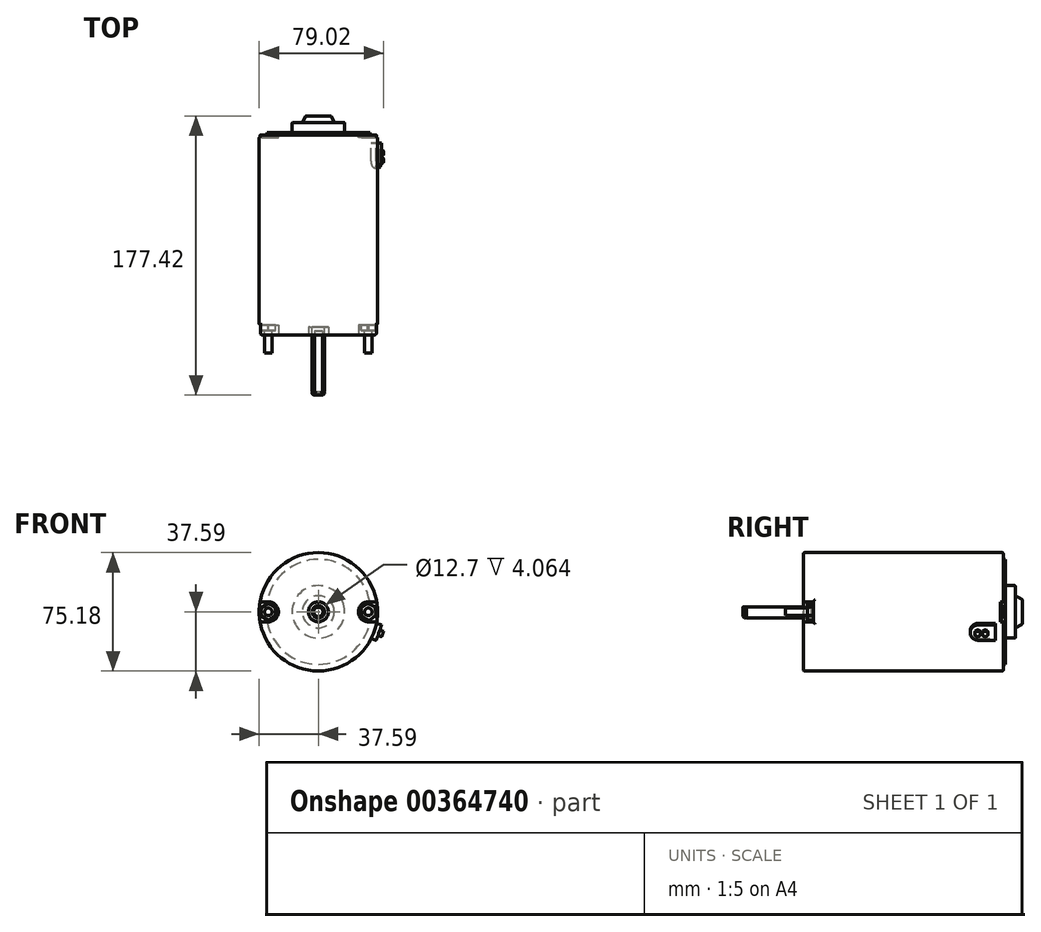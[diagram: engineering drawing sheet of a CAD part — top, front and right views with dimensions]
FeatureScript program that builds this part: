
annotation { "Feature Type Name" : "Feature", "Feature Type Description" : "" }
export const myFeature = defineFeature(function(context is Context, id is Id, definition is map)
    precondition{}
    {
        {
            var Q0;
            Q0=qCreatedBy(makeId("Front.planeOp"),FACE);
            var sketch = newSketch(context, id + "F0", { "sketchPlane" : qUnion([Q0])});
            skCircle(sketch, "E0", {"center": v(0, 0) * mm, "radius": 37.6 * mm});
            skSolve(sketch);
        }
        {
            var Q0;
            Q0 = qSketchRegion(id + "F0", true);
            extrude(context, id + "F1", {"entities" : qUnion([Q0]), "depth" : 127 * mm});
        }
        {
            var Q0;
            Q0=makeQuery(id+"F1.opExtrude","CAP_FACE",FACE,{"disambiguationData":[OSD([sQuery(id+"F0.wireOp",EDGE,"E0")])],"isStart":false});
            var sketch = newSketch(context, id + "F2", { "sketchPlane" : qUnion([Q0])});
            skCircle(sketch, "E1", {"center": v(0, 0) * mm, "radius": 6.35 * mm});
            skSolve(sketch);
        }
        {
            var Q0;
            Q0 = qSketchRegion(id + "F2", true);
            extrude(context, id + "F3", {"entities" : qUnion([Q0]), "operationType" : NewBodyOperationType.REMOVE, "oppositeDirection" : true, "depth" : 5.08 * mm});
        }
        {
            var Q0;
            Q0=makeQuery(id+"F3.boolean.opBoolean","COPY",FACE,{"derivedFrom":makeQuery(id+"F3.opExtrude","CAP_FACE",FACE,{"disambiguationData":[OSD([sQuery(id+"F2.wireOp",EDGE,"E1")])],"isStart":false})});
            var sketch = newSketch(context, id + "F4", { "sketchPlane" : qUnion([Q0])});
            skCircle(sketch, "E2", {"center": v(0, 0) * mm, "radius": 3.96 * mm});
            skSolve(sketch);
        }
        {
            var Q0;
            Q0 = qSketchRegion(id + "F4", true);
            extrude(context, id + "F5", {"entities" : qUnion([Q0]), "operationType" : NewBodyOperationType.ADD, "depth" : 43.43 * mm});
        }
        {
            var Q0;
            Q0=makeQuery(id+"F5.opExtrude","CAP_EDGE",EDGE,{"disambiguationData":[OSD([sQuery(id+"F4.wireOp",EDGE,"E2")])],"isStart":false});
            chamfer(context, id + "F6", {"entities" : qUnion([Q0]), "width" : 1.02 * mm, "tangentPropagation" : true});
        }
        {
            var Q0;
            Q0=makeQuery(id+"F5.opExtrude","CAP_FACE",FACE,{"disambiguationData":[OSD([sQuery(id+"F4.wireOp",EDGE,"E2")])],"isStart":false});
            var sketch = newSketch(context, id + "F7", { "sketchPlane" : qUnion([Q0])});
            skLineSegment(sketch, "E3", {"start": v(-2.56, 3.02) * mm, "end": v(2.56, 3.02) * mm});
            skArc(sketch, "E4.0", {"start": v(2.56, 3.02) * mm, "mid": v(0, 3.96) * mm, "end": v(-2.56, 3.02) * mm});
            skLineSegment(sketch, "E5", {"start": v(0, 3.02) * mm, "end": v(0, -3.96) * mm, "construction": true});
            skPoint(sketch, "E6.orphan", {"position": v(-4.9, 3.02) * mm});
            skPoint(sketch, "E7.orphan", {"position": v(4.9, 3.02) * mm});
            skSolve(sketch);
        }
        {
            var Q0;
            Q0 = qSketchRegion(id + "F7", true);
            var Q1;
            Q1=makeQuery(id+"F3.boolean.opBoolean","COPY",FACE,{"derivedFrom":makeQuery(id+"F3.opExtrude","CAP_FACE",FACE,{"disambiguationData":[OSD([sQuery(id+"F2.wireOp",EDGE,"E1")])],"isStart":false})});
            extrude(context, id + "F8", {"entities" : qUnion([Q0]), "operationType" : NewBodyOperationType.REMOVE, "oppositeDirection" : true, "endBoundEntityFace" : qUnion([Q1]), "depth" : 40.64 * mm});
        }
        {
            var Q0;
            Q0=makeQuery(id+"F5.opExtrude","CAP_FACE",FACE,{"disambiguationData":[OSD([sQuery(id+"F4.wireOp",EDGE,"E2")])],"isStart":false});
            cPlane(context, id + "F9", {"entities" : qUnion([Q0]), "cplaneType" : CPlaneType.OFFSET, "offset" : 1.6 * mm, "oppositeDirection" : true, "width" : 152.4 * mm, "height" : 152.4 * mm});
        }
        {
            var Q0;
            Q0=qCreatedBy(id+"F9.planeOp",FACE);
            var sketch = newSketch(context, id + "F10", { "sketchPlane" : qUnion([Q0])});
            skCircle(sketch, "E8", {"center": v(0, 0) * mm, "radius": 3.58 * mm});
            skCircle(sketch, "E9", {"center": v(0, 0) * mm, "radius": 4.9 * mm});
            skSolve(sketch);
        }
        {
            var Q0;
            Q0 = qSketchRegion(id + "F10", true);
            extrude(context, id + "F11", {"entities" : qUnion([Q0]), "operationType" : NewBodyOperationType.REMOVE, "oppositeDirection" : true, "depth" : 0.79 * mm});
        }
        {
            var Q0;
            Q0=makeQuery(id+"F1.opExtrude","CAP_FACE",FACE,{"disambiguationData":[OSD([sQuery(id+"F0.wireOp",EDGE,"E0")])],"isStart":false});
            var sketch = newSketch(context, id + "F12", { "sketchPlane" : qUnion([Q0])});
            skArc(sketch, "E10", {"start": v(31.75, 6.35) * mm, "mid": v(25.4, 0) * mm, "end": v(31.75, -6.35) * mm});
            skArc(sketch, "E11", {"start": v(-31.75, -6.35) * mm, "mid": v(-25.4, 0) * mm, "end": v(-31.75, 6.35) * mm});
            skLineSegment(sketch, "E12", {"start": v(-31.75, 0) * mm, "end": v(31.75, 0) * mm, "construction": true});
            skLineSegment(sketch, "E13", {"start": v(-31.75, -6.35) * mm, "end": v(-52.48, -6.35) * mm});
            skLineSegment(sketch, "E14", {"start": v(-52.48, -6.35) * mm, "end": v(-52.48, 6.35) * mm});
            skLineSegment(sketch, "E15", {"start": v(-52.48, 6.35) * mm, "end": v(-31.75, 6.35) * mm});
            skLineSegment(sketch, "E16", {"start": v(31.75, -6.35) * mm, "end": v(43.63, -6.35) * mm});
            skLineSegment(sketch, "E17", {"start": v(43.63, -6.35) * mm, "end": v(43.63, 6.35) * mm});
            skLineSegment(sketch, "E18", {"start": v(43.63, 6.35) * mm, "end": v(31.75, 6.35) * mm});
            skSolve(sketch);
        }
        {
            var Q0;
            Q0 = qSketchRegion(id + "F12", true);
            extrude(context, id + "F13", {"entities" : qUnion([Q0]), "operationType" : NewBodyOperationType.REMOVE, "oppositeDirection" : true, "depth" : 6.35 * mm});
        }
        {
            var Q0;
            Q0=makeQuery(id+"F1.opExtrude","CAP_FACE",FACE,{"disambiguationData":[OSD([sQuery(id+"F0.wireOp",EDGE,"E0")])],"isStart":false});
            fillet(context, id + "F14", {"entities" : qUnion([Q0]), "radius" : 1.02 * mm, "tangentPropagation" : true, "allowEdgeOverflow" : false});
        }
        {
            var Q0;
            Q0=makeQuery(id+"F13.boolean.opBoolean","INTERSECT",EDGE,{"derivedFrom":[makeQuery(id+"F1.opExtrude","SWEPT_FACE",FACE,{"disambiguationData":[OSD([sQuery(id+"F0.wireOp",EDGE,"E0")])]}),makeQuery(id+"F13.opExtrude","CAP_FACE",FACE,{"disambiguationData":[OSD([sQuery(id+"F12.wireOp",EDGE,"E11"),sQuery(id+"F12.wireOp",EDGE,"E13"),sQuery(id+"F12.wireOp",EDGE,"E14"),sQuery(id+"F12.wireOp",EDGE,"E15")])],"isStart":false})]});
            var Q1;
            Q1=makeQuery(id+"F13.boolean.opBoolean","INTERSECT",EDGE,{"derivedFrom":[makeQuery(id+"F1.opExtrude","SWEPT_FACE",FACE,{"disambiguationData":[OSD([sQuery(id+"F0.wireOp",EDGE,"E0")])]}),makeQuery(id+"F13.opExtrude","SWEPT_FACE",FACE,{"disambiguationData":[OSD([sQuery(id+"F12.wireOp",EDGE,"E15")])]})]});
            var Q2;
            Q2=makeQuery(id+"F13.boolean.opBoolean","INTERSECT",EDGE,{"derivedFrom":[makeQuery(id+"F1.opExtrude","SWEPT_FACE",FACE,{"disambiguationData":[OSD([sQuery(id+"F0.wireOp",EDGE,"E0")])]}),makeQuery(id+"F13.opExtrude","SWEPT_FACE",FACE,{"disambiguationData":[OSD([sQuery(id+"F12.wireOp",EDGE,"E13")])]})]});
            var Q3;
            Q3=makeQuery(id+"F13.boolean.opBoolean","INTERSECT",EDGE,{"derivedFrom":[makeQuery(id+"F1.opExtrude","SWEPT_FACE",FACE,{"disambiguationData":[OSD([sQuery(id+"F0.wireOp",EDGE,"E0")])]}),makeQuery(id+"F13.opExtrude","SWEPT_FACE",FACE,{"disambiguationData":[OSD([sQuery(id+"F12.wireOp",EDGE,"E16")])]})]});
            var Q4;
            Q4=makeQuery(id+"F13.boolean.opBoolean","INTERSECT",EDGE,{"derivedFrom":[makeQuery(id+"F1.opExtrude","SWEPT_FACE",FACE,{"disambiguationData":[OSD([sQuery(id+"F0.wireOp",EDGE,"E0")])]}),makeQuery(id+"F13.opExtrude","CAP_FACE",FACE,{"disambiguationData":[OSD([sQuery(id+"F12.wireOp",EDGE,"E10"),sQuery(id+"F12.wireOp",EDGE,"E16"),sQuery(id+"F12.wireOp",EDGE,"E17"),sQuery(id+"F12.wireOp",EDGE,"E18")])],"isStart":false})]});
            var Q5;
            Q5=makeQuery(id+"F13.boolean.opBoolean","INTERSECT",EDGE,{"derivedFrom":[makeQuery(id+"F1.opExtrude","SWEPT_FACE",FACE,{"disambiguationData":[OSD([sQuery(id+"F0.wireOp",EDGE,"E0")])]}),makeQuery(id+"F13.opExtrude","SWEPT_FACE",FACE,{"disambiguationData":[OSD([sQuery(id+"F12.wireOp",EDGE,"E18")])]})]});
            fillet(context, id + "F15", {"entities" : qUnion([Q0, Q1, Q2, Q3, Q4, Q5]), "radius" : 1.02 * mm, "tangentPropagation" : true, "allowEdgeOverflow" : false});
        }
        {
            var Q0;
            Q0=makeQuery(id+"F13.boolean.opBoolean","COPY",FACE,{"derivedFrom":makeQuery(id+"F13.opExtrude","CAP_FACE",FACE,{"disambiguationData":[OSD([sQuery(id+"F12.wireOp",EDGE,"E11"),sQuery(id+"F12.wireOp",EDGE,"E13"),sQuery(id+"F12.wireOp",EDGE,"E14"),sQuery(id+"F12.wireOp",EDGE,"E15")])],"isStart":false})});
            var sketch = newSketch(context, id + "F16", { "sketchPlane" : qUnion([Q0])});
            skCircle(sketch, "E19", {"center": v(-31.75, 0) * mm, "radius": 2.37 * mm});
            skCircle(sketch, "E20", {"center": v(31.75, 0) * mm, "radius": 2.37 * mm});
            skSolve(sketch);
        }
        {
            var Q0;
            Q0 = qSketchRegion(id + "F16", true);
            extrude(context, id + "F17", {"entities" : qUnion([Q0]), "operationType" : NewBodyOperationType.ADD, "depth" : 17.78 * mm});
        }
        {
            var Q0;
            Q0=makeQuery(id+"F13.boolean.opBoolean","COPY",FACE,{"derivedFrom":makeQuery(id+"F13.opExtrude","CAP_FACE",FACE,{"disambiguationData":[OSD([sQuery(id+"F12.wireOp",EDGE,"E11"),sQuery(id+"F12.wireOp",EDGE,"E13"),sQuery(id+"F12.wireOp",EDGE,"E14"),sQuery(id+"F12.wireOp",EDGE,"E15")])],"isStart":false})});
            var sketch = newSketch(context, id + "F18", { "sketchPlane" : qUnion([Q0])});
            skCircle(sketch, "E21.cCircle", {"center": v(-31.75, 0) * mm, "radius": 5.33 * mm, "construction": true});
            skLineSegment(sketch, "E21.0", {"start": v(-36.4, 2.6) * mm, "end": v(-31.82, 5.33) * mm});
            skLineSegment(sketch, "E21.1", {"start": v(-31.82, 5.33) * mm, "end": v(-27.17, 2.73) * mm});
            skLineSegment(sketch, "E21.2", {"start": v(-27.17, 2.73) * mm, "end": v(-27.1, -2.6) * mm});
            skLineSegment(sketch, "E21.3", {"start": v(-27.1, -2.6) * mm, "end": v(-31.68, -5.33) * mm});
            skLineSegment(sketch, "E21.4", {"start": v(-31.68, -5.33) * mm, "end": v(-36.33, -2.73) * mm});
            skLineSegment(sketch, "E21.5", {"start": v(-36.33, -2.73) * mm, "end": v(-36.4, 2.6) * mm});
            skCircle(sketch, "E22.cCircle", {"center": v(31.75, 0) * mm, "radius": 5.33 * mm, "construction": true});
            skLineSegment(sketch, "E22.0", {"start": v(36.55, -2.33) * mm, "end": v(32.13, -5.32) * mm});
            skLineSegment(sketch, "E22.1", {"start": v(32.13, -5.32) * mm, "end": v(27.33, -2.99) * mm});
            skLineSegment(sketch, "E22.2", {"start": v(27.33, -2.99) * mm, "end": v(26.95, 2.33) * mm});
            skLineSegment(sketch, "E22.3", {"start": v(26.95, 2.33) * mm, "end": v(31.37, 5.32) * mm});
            skLineSegment(sketch, "E22.4", {"start": v(31.37, 5.32) * mm, "end": v(36.17, 2.99) * mm});
            skLineSegment(sketch, "E22.5", {"start": v(36.17, 2.99) * mm, "end": v(36.55, -2.33) * mm});
            skSolve(sketch);
        }
        {
            var Q0;
            Q0 = qSketchRegion(id + "F18", true);
            extrude(context, id + "F19", {"entities" : qUnion([Q0]), "operationType" : NewBodyOperationType.ADD, "depth" : 3.68 * mm});
        }
        {
            var Q0;
            Q0=makeQuery(id+"F1.opExtrude","CAP_FACE",FACE,{"disambiguationData":[OSD([sQuery(id+"F0.wireOp",EDGE,"E0")])],"isStart":true});
            var sketch = newSketch(context, id + "F20", { "sketchPlane" : qUnion([Q0])});
            skCircle(sketch, "E23", {"center": v(0, 0) * mm, "radius": 33.34 * mm});
            skSolve(sketch);
        }
        {
            var Q0;
            Q0 = qSketchRegion(id + "F20", true);
            extrude(context, id + "F21", {"entities" : qUnion([Q0]), "operationType" : NewBodyOperationType.ADD, "depth" : 1.52 * mm});
        }
        {
            var Q0;
            Q0=makeQuery(id+"F21.opExtrude","CAP_FACE",FACE,{"disambiguationData":[OSD([sQuery(id+"F20.wireOp",EDGE,"E23")])],"isStart":false});
            var sketch = newSketch(context, id + "F22", { "sketchPlane" : qUnion([Q0])});
            skCircle(sketch, "E24", {"center": v(0, 0) * mm, "radius": 16.64 * mm});
            skSolve(sketch);
        }
        {
            var Q0;
            Q0 = qSketchRegion(id + "F22", true);
            extrude(context, id + "F23", {"entities" : qUnion([Q0]), "operationType" : NewBodyOperationType.ADD, "depth" : 6.35 * mm});
        }
        {
            var Q0;
            Q0=makeQuery(id+"F23.opExtrude","CAP_FACE",FACE,{"disambiguationData":[OSD([sQuery(id+"F22.wireOp",EDGE,"E24")])],"isStart":false});
            var sketch = newSketch(context, id + "F24", { "sketchPlane" : qUnion([Q0])});
            skCircle(sketch, "E25", {"center": v(0, 0) * mm, "radius": 10.16 * mm});
            skSolve(sketch);
        }
        {
            var Q0;
            Q0 = qSketchRegion(id + "F24", true);
            extrude(context, id + "F25", {"entities" : qUnion([Q0]), "operationType" : NewBodyOperationType.ADD, "depth" : 4.2 * mm});
        }
        {
            var Q0;
            Q0=makeQuery(id+"F25.opExtrude","CAP_EDGE",EDGE,{"disambiguationData":[OSD([sQuery(id+"F24.wireOp",EDGE,"E25")])],"isStart":false});
            chamfer(context, id + "F26", {"entities" : qUnion([Q0]), "chamferType" : ChamferType.TWO_OFFSETS, "width1" : 2.3 * mm, "oppositeDirection" : false, "width2" : 4.2 * mm, "tangentPropagation" : true});
        }
        {
            var Q0;
            {var subQ0=sQuery(id+"F24.wireOp",EDGE,"E25");Q0=makeQuery(id+"F26.opChamfer","BLEND_EDGE",EDGE,{"blendedFrom":[makeQuery(id+"F25.opExtrude","CAP_EDGE",EDGE,{"disambiguationData":[OSD([subQ0])],"isStart":false}),makeQuery(id+"F25.opExtrude","CAP_FACE",FACE,{"disambiguationData":[OSD([subQ0])],"isStart":false})],"blendedInto":[makeQuery(id+"F25.opExtrude","CAP_FACE",FACE,{"disambiguationData":[OSD([subQ0])],"isStart":false})]});}
            var Q1;
            Q1=makeQuery(id+"F23.opExtrude","CAP_EDGE",EDGE,{"disambiguationData":[OSD([sQuery(id+"F22.wireOp",EDGE,"E24")])],"isStart":false});
            var Q2;
            Q2=makeQuery(id+"F1.opExtrude","CAP_EDGE",EDGE,{"disambiguationData":[OSD([sQuery(id+"F0.wireOp",EDGE,"E0")])],"isStart":true});
            fillet(context, id + "F27", {"entities" : qUnion([Q0, Q1, Q2]), "radius" : 0.5 * mm, "tangentPropagation" : true, "allowEdgeOverflow" : false});
        }
        {
            var Q0;
            Q0=makeQuery(id+"F21.opExtrude","CAP_FACE",FACE,{"disambiguationData":[OSD([sQuery(id+"F20.wireOp",EDGE,"E23")])],"isStart":false});
            var sketch = newSketch(context, id + "F28", { "sketchPlane" : qUnion([Q0])});
            skArc(sketch, "E26", {"start": v(-31.75, -6.35) * mm, "mid": v(-25.4, 0) * mm, "end": v(-31.75, 6.35) * mm});
            skArc(sketch, "E27", {"start": v(31.75, 6.35) * mm, "mid": v(25.4, 0) * mm, "end": v(31.75, -6.35) * mm});
            skLineSegment(sketch, "E28", {"start": v(-31.75, 0) * mm, "end": v(31.75, 0) * mm});
            skLineSegment(sketch, "E29", {"start": v(-31.75, -6.35) * mm, "end": v(-50.26, -6.35) * mm});
            skLineSegment(sketch, "E30", {"start": v(-50.26, -6.35) * mm, "end": v(-50.26, 6.35) * mm});
            skLineSegment(sketch, "E31", {"start": v(-50.26, 6.35) * mm, "end": v(-31.75, 6.35) * mm});
            skLineSegment(sketch, "E32", {"start": v(31.75, 6.35) * mm, "end": v(48.33, 6.35) * mm});
            skLineSegment(sketch, "E33", {"start": v(48.33, 6.35) * mm, "end": v(48.33, -6.35) * mm});
            skLineSegment(sketch, "E34", {"start": v(48.33, -6.35) * mm, "end": v(31.75, -6.35) * mm});
            skSolve(sketch);
        }
        {
            var Q0;
            Q0 = qSketchRegion(id + "F28", true);
            extrude(context, id + "F29", {"entities" : qUnion([Q0]), "operationType" : NewBodyOperationType.REMOVE, "oppositeDirection" : true, "depth" : 3.17 * mm});
        }
        {
            var Q0;
            Q0=makeQuery(id+"F29.boolean.opBoolean","COPY",FACE,{"derivedFrom":makeQuery(id+"F29.opExtrude","CAP_FACE",FACE,{"disambiguationData":[OSD([sQuery(id+"F28.wireOp",EDGE,"E27"),sQuery(id+"F28.wireOp",EDGE,"E32"),sQuery(id+"F28.wireOp",EDGE,"E33"),sQuery(id+"F28.wireOp",EDGE,"E34")])],"isStart":false})});
            var sketch = newSketch(context, id + "F30", { "sketchPlane" : qUnion([Q0])});
            skCircle(sketch, "E35", {"center": v(31.75, 0) * mm, "radius": 4.25 * mm});
            skCircle(sketch, "E36", {"center": v(-31.75, 0) * mm, "radius": 4.25 * mm});
            skSolve(sketch);
        }
        {
            var Q0;
            Q0 = qSketchRegion(id + "F30", true);
            extrude(context, id + "F31", {"entities" : qUnion([Q0]), "operationType" : NewBodyOperationType.ADD, "depth" : 1.4 * mm});
        }
        {
            var Q0;
            Q0=makeQuery(id+"F29.boolean.opBoolean","COPY",FACE,{"derivedFrom":makeQuery(id+"F29.opExtrude","CAP_FACE",FACE,{"disambiguationData":[OSD([sQuery(id+"F28.wireOp",EDGE,"E26"),sQuery(id+"F28.wireOp",EDGE,"E29"),sQuery(id+"F28.wireOp",EDGE,"E30"),sQuery(id+"F28.wireOp",EDGE,"E31")])],"isStart":false})});
            var sketch = newSketch(context, id + "F32", { "sketchPlane" : qUnion([Q0])});
            skLineSegment(sketch, "E37", {"start": v(0, 0) * mm, "end": v(-38.43, -13.23) * mm});
            skLineSegment(sketch, "E38", {"start": v(0, 0) * mm, "end": v(-49.41, 0) * mm, "construction": true});
            skLineSegment(sketch, "E39", {"start": v(-40.08, -8.43) * mm, "end": v(-36.77, -18.03) * mm});
            skLineSegment(sketch, "E40", {"start": v(-40.08, -8.43) * mm, "end": v(-33.03, -6) * mm});
            skLineSegment(sketch, "E41", {"start": v(-33.03, -6) * mm, "end": v(-29.72, -15.6) * mm});
            skLineSegment(sketch, "E42", {"start": v(-29.72, -15.6) * mm, "end": v(-36.77, -18.03) * mm});
            skSolve(sketch);
        }
        {
            var Q0;
            Q0 = qSketchRegion(id + "F32", true);
            extrude(context, id + "F33", {"entities" : qUnion([Q0]), "operationType" : NewBodyOperationType.ADD, "oppositeDirection" : true, "depth" : 19.3 * mm});
        }
        {
            var Q0;
            Q0=makeQuery(id+"F33.opExtrude","SWEPT_FACE",FACE,{"disambiguationData":[OSD([sQuery(id+"F32.wireOp",EDGE,"E39")])]});
            var sketch = newSketch(context, id + "F34", { "sketchPlane" : qUnion([Q0])});
            skArc(sketch, "E43", {"start": v(-15.87, 5.08) * mm, "mid": v(-20.96, 0) * mm, "end": v(-15.87, -5.08) * mm});
            skLineSegment(sketch, "E44.0", {"start": v(0, 5.9) * mm, "end": v(0, -37.08) * mm, "construction": true});
            skLineSegment(sketch, "E45.0", {"start": v(-15.87, -5.08) * mm, "end": v(-5.08, -5.08) * mm});
            skLineSegment(sketch, "E45.1", {"start": v(-20.96, 5.08) * mm, "end": v(-20.96, -5.08) * mm, "construction": true});
            skLineSegment(sketch, "E45.2", {"start": v(-15.87, 5.08) * mm, "end": v(-5.08, 5.08) * mm});
            skLineSegment(sketch, "E46", {"start": v(-5.08, -5.08) * mm, "end": v(-5.08, 5.08) * mm});
            skLineSegment(sketch, "E47.bottom", {"start": v(-26.14, -11.18) * mm, "end": v(4.57, -11.18) * mm});
            skLineSegment(sketch, "E47.top", {"start": v(-26.14, 9.91) * mm, "end": v(4.57, 9.91) * mm});
            skLineSegment(sketch, "E47.left", {"start": v(-26.14, -11.18) * mm, "end": v(-26.14, 9.91) * mm});
            skLineSegment(sketch, "E47.right", {"start": v(4.57, -11.18) * mm, "end": v(4.57, 9.91) * mm});
            skSolve(sketch);
        }
        {
            var Q0;
            {var subQ0=sQuery(id+"F34.wireOp",EDGE,"E43");var subQ1=sQuery(id+"F32.wireOp",EDGE,"E39");var subQ4=makeQuery(id+"F33.opExtrude","CAP_EDGE",EDGE,{"disambiguationData":[OSD([subQ1])],"isStart":false});var subQ5=makeQuery(id+"F34.imprint","INTERSECT",VERTEX,{"derivedFrom":[subQ4,subQ0]});Q0=makeQuery(id+"F34.imprint","IMPRINT",FACE,{"disambiguationData":[TD([[makeQuery(id+"F34.imprint","IMPRINT",EDGE,{"disambiguationData":[TD([[subQ5,-1.0]])],"derivedFrom":subQ4}),1.0]])]});}
            var Q1;
            {var subQ4=sQuery(id+"F34.wireOp",EDGE,"E45.0");Q1=makeQuery(id+"F34.imprint","IMPRINT",FACE,{"disambiguationData":[TD([[makeQuery(id+"F34.imprint","IMPRINT",EDGE,{"derivedFrom":subQ4}),-1.0]])]});}
            var Q2;
            {var subQ0=sQuery(id+"F34.wireOp",EDGE,"E43");var subQ1=sQuery(id+"F32.wireOp",EDGE,"E39");var subQ4=makeQuery(id+"F33.opExtrude","CAP_EDGE",EDGE,{"disambiguationData":[OSD([subQ1])],"isStart":false});var subQ5=makeQuery(id+"F34.imprint","INTERSECT",VERTEX,{"derivedFrom":[subQ4,subQ0]});Q2=makeQuery(id+"F34.imprint","IMPRINT",FACE,{"disambiguationData":[TD([[makeQuery(id+"F34.imprint","IMPRINT",EDGE,{"disambiguationData":[TD([[subQ5,1.0]])],"derivedFrom":subQ4}),1.0]])]});}
            var Q3;
            {var subQ0=sQuery(id+"F34.wireOp",EDGE,"E46");Q3=makeQuery(id+"F34.imprint","IMPRINT",FACE,{"disambiguationData":[TD([[makeQuery(id+"F34.imprint","IMPRINT",EDGE,{"derivedFrom":subQ0}),-1.0]])]});}
            var Q4;
            Q4=makeQuery(id+"F1.opExtrude","SWEPT_FACE",FACE,{"disambiguationData":[OSD([sQuery(id+"F0.wireOp",EDGE,"E0")])]});
            extrude(context, id + "F35", {"entities" : qUnion([Q0, Q1, Q2, Q3]), "operationType" : NewBodyOperationType.REMOVE, "endBound" : BoundingType.UP_TO_SURFACE, "oppositeDirection" : true, "endBoundEntityFace" : qUnion([Q4]), "depth" : 2.54 * mm});
        }
        {
            var Q0;
            Q0=makeQuery(id+"F33.opExtrude","SWEPT_FACE",FACE,{"disambiguationData":[OSD([sQuery(id+"F32.wireOp",EDGE,"E39")])]});
            var sketch = newSketch(context, id + "F36", { "sketchPlane" : qUnion([Q0])});
            skCircle(sketch, "E48", {"center": v(-16.18, 0) * mm, "radius": 1.84 * mm});
            skCircle(sketch, "E49", {"center": v(-11.43, 0) * mm, "radius": 1.84 * mm});
            skSolve(sketch);
        }
        {
            var Q0;
            Q0 = qSketchRegion(id + "F36", true);
            extrude(context, id + "F37", {"entities" : qUnion([Q0]), "operationType" : NewBodyOperationType.ADD, "depth" : 2.54 * mm});
        }
    });
